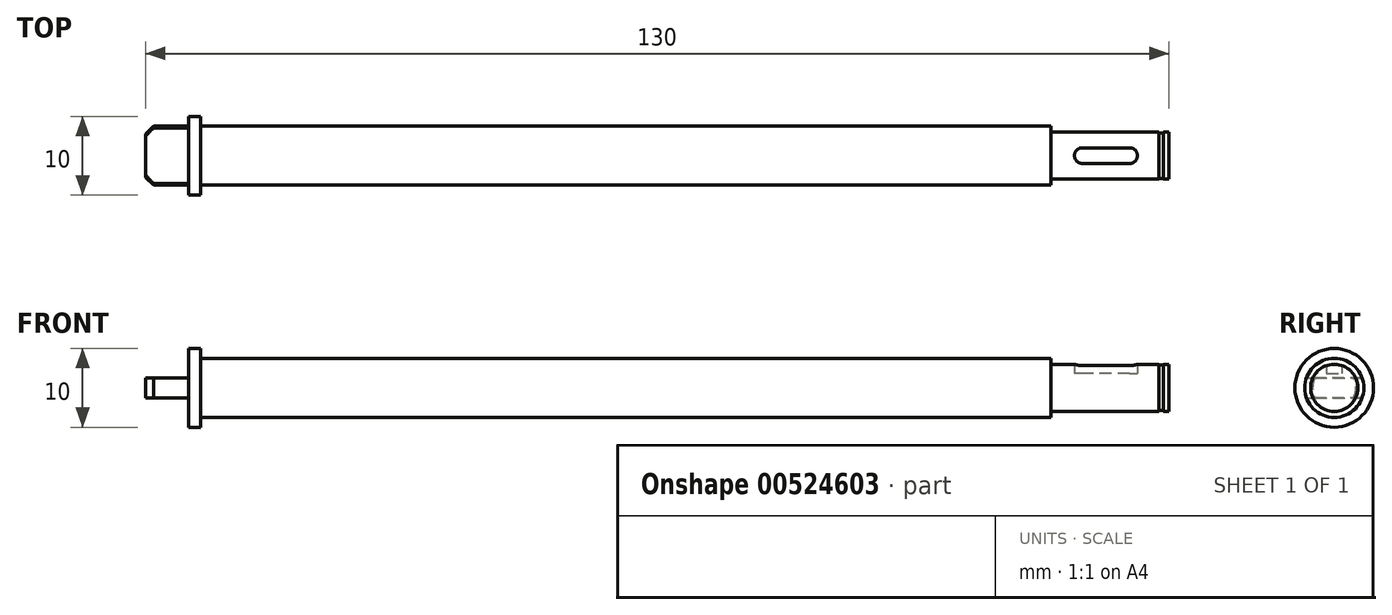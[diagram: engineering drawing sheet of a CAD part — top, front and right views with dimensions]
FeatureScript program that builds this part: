
annotation { "Feature Type Name" : "Feature", "Feature Type Description" : "" }
export const myFeature = defineFeature(function(context is Context, id is Id, definition is map)
    precondition{}
    {
        {
            var Q0;
            Q0=qCreatedBy(makeId("Front.planeOp"),FACE);
            var sketch = newSketch(context, id + "F0", { "sketchPlane" : qUnion([Q0])});
            skLineSegment(sketch, "E0", {"start": v(-31.25, 0) * mm, "end": v(193.53, 0) * mm, "construction": true});
            skLineSegment(sketch, "E1", {"start": v(0, 0) * mm, "end": v(0, 3.75) * mm});
            skLineSegment(sketch, "E2", {"start": v(0, 3.75) * mm, "end": v(5.5, 3.75) * mm});
            skLineSegment(sketch, "E3", {"start": v(5.5, 3.75) * mm, "end": v(5.5, 5) * mm});
            skLineSegment(sketch, "E4", {"start": v(5.5, 5) * mm, "end": v(7, 5) * mm});
            skLineSegment(sketch, "E5", {"start": v(7, 5) * mm, "end": v(7, 3.75) * mm});
            skLineSegment(sketch, "E6", {"start": v(7, 3.75) * mm, "end": v(115, 3.75) * mm});
            skLineSegment(sketch, "E7", {"start": v(115, 3.75) * mm, "end": v(115, 3) * mm});
            skLineSegment(sketch, "E8", {"start": v(115, 3) * mm, "end": v(128.7, 3) * mm});
            skLineSegment(sketch, "E9", {"start": v(128.7, 3) * mm, "end": v(128.7, 2.9) * mm});
            skLineSegment(sketch, "E10", {"start": v(128.7, 2.9) * mm, "end": v(129.3, 2.9) * mm});
            skLineSegment(sketch, "E11", {"start": v(129.3, 2.9) * mm, "end": v(129.3, 3) * mm});
            skLineSegment(sketch, "E12", {"start": v(129.3, 3) * mm, "end": v(130, 3) * mm});
            skLineSegment(sketch, "E13", {"start": v(130, 3) * mm, "end": v(130, 0) * mm});
            skLineSegment(sketch, "E14", {"start": v(130, 0) * mm, "end": v(0, 0) * mm});
            skSolve(sketch);
        }
        {
            var Q0;
            Q0 = qSketchRegion(id + "F0", true);
            var Q1;
            Q1=sQuery(id+"F0.wireOp",EDGE,"E0");
            revolve(context, id + "F1", {"entities" : qUnion([Q0]), "axis" : qUnion([Q1]), "revolveType" : RevolveType.FULL});
        }
        {
            var Q0;
            Q0=makeQuery(id+"F1.opRevolve","SWEPT_EDGE",EDGE,{"disambiguationData":[OSD([sQuery(id+"F0.wireOp",EDGE,"E1"),sQuery(id+"F0.wireOp",EDGE,"E2")])]});
            chamfer(context, id + "F2", {"entities" : qUnion([Q0]), "width" : 1 * mm, "tangentPropagation" : true});
        }
        {
            var Q0;
            Q0=makeQuery(id+"F1.opRevolve","SWEPT_FACE",FACE,{"disambiguationData":[OSD([sQuery(id+"F0.wireOp",EDGE,"E1")])]});
            var sketch = newSketch(context, id + "F3", { "sketchPlane" : qUnion([Q0])});
            skCircle(sketch, "E15.0", {"center": v(0, 0) * mm, "radius": 3.75 * mm});
            skLineSegment(sketch, "E16.bottom", {"start": v(3.54, 1.25) * mm, "end": v(-3.54, 1.25) * mm});
            skLineSegment(sketch, "E16.top", {"start": v(3.54, -1.25) * mm, "end": v(-3.54, -1.25) * mm});
            skSolve(sketch);
        }
        {
            var Q0;
            {var subQ0=sQuery(id+"F3.wireOp",EDGE,"E16.bottom");var subQ1=sQuery(id+"F0.wireOp",EDGE,"E1");var subQ2=makeQuery(id+"F2.opChamfer","BLEND_EDGE",EDGE,{"blendedFrom":[makeQuery(id+"F1.opRevolve","SWEPT_EDGE",EDGE,{"disambiguationData":[OSD([subQ1,sQuery(id+"F0.wireOp",EDGE,"E2")])]}),makeQuery(id+"F1.opRevolve","SWEPT_FACE",FACE,{"disambiguationData":[OSD([subQ1])]})],"blendedInto":[makeQuery(id+"F1.opRevolve","SWEPT_FACE",FACE,{"disambiguationData":[OSD([subQ1])]})]});var subQ3=makeQuery(id+"F3.imprint","INTERSECT",VERTEX,{"disambiguationData":[OD(0.0)],"derivedFrom":[subQ2,subQ0]});Q0=makeQuery(id+"F3.imprint","IMPRINT",FACE,{"disambiguationData":[TD([[makeQuery(id+"F3.imprint","IMPRINT",EDGE,{"disambiguationData":[TD([[subQ3,-1.0]])],"derivedFrom":subQ0}),-1.0]])]});}
            var Q1;
            {var subQ0=sQuery(id+"F3.wireOp",EDGE,"E16.top");var subQ1=sQuery(id+"F0.wireOp",EDGE,"E1");var subQ2=makeQuery(id+"F2.opChamfer","BLEND_EDGE",EDGE,{"blendedFrom":[makeQuery(id+"F1.opRevolve","SWEPT_EDGE",EDGE,{"disambiguationData":[OSD([subQ1,sQuery(id+"F0.wireOp",EDGE,"E2")])]}),makeQuery(id+"F1.opRevolve","SWEPT_FACE",FACE,{"disambiguationData":[OSD([subQ1])]})],"blendedInto":[makeQuery(id+"F1.opRevolve","SWEPT_FACE",FACE,{"disambiguationData":[OSD([subQ1])]})]});var subQ3=makeQuery(id+"F3.imprint","INTERSECT",VERTEX,{"disambiguationData":[OD(0.0)],"derivedFrom":[subQ2,subQ0]});Q1=makeQuery(id+"F3.imprint","IMPRINT",FACE,{"disambiguationData":[TD([[makeQuery(id+"F3.imprint","IMPRINT",EDGE,{"disambiguationData":[TD([[subQ3,-1.0]])],"derivedFrom":subQ0}),1.0]])]});}
            var Q2;
            {var subQ0=sQuery(id+"F3.wireOp",EDGE,"E16.top");var subQ1=sQuery(id+"F3.wireOp",EDGE,"E15.0");var subQ2=makeQuery(id+"F3.imprint","INTERSECT",VERTEX,{"disambiguationData":[OD(0.0)],"derivedFrom":[subQ1,subQ0]});Q2=makeQuery(id+"F3.imprint","IMPRINT",FACE,{"disambiguationData":[TD([[makeQuery(id+"F3.imprint","IMPRINT",EDGE,{"disambiguationData":[TD([[subQ2,1.0]])],"derivedFrom":subQ1}),1.0]])]});}
            var Q3;
            {var subQ0=sQuery(id+"F3.wireOp",EDGE,"E16.bottom");var subQ1=sQuery(id+"F3.wireOp",EDGE,"E15.0");var subQ2=makeQuery(id+"F3.imprint","INTERSECT",VERTEX,{"disambiguationData":[OD(0.0)],"derivedFrom":[subQ1,subQ0]});Q3=makeQuery(id+"F3.imprint","IMPRINT",FACE,{"disambiguationData":[TD([[makeQuery(id+"F3.imprint","IMPRINT",EDGE,{"disambiguationData":[TD([[subQ2,-1.0]])],"derivedFrom":subQ1}),1.0]])]});}
            var Q4;
            Q4=makeQuery(id+"F1.opRevolve","SWEPT_FACE",FACE,{"disambiguationData":[OSD([sQuery(id+"F0.wireOp",EDGE,"E3")])]});
            extrude(context, id + "F4", {"entities" : qUnion([Q0, Q1, Q2, Q3]), "operationType" : NewBodyOperationType.REMOVE, "endBound" : BoundingType.UP_TO_SURFACE, "oppositeDirection" : true, "depth" : 25 * mm, "endBoundEntityFace" : qUnion([Q4]), "offsetDistance" : 25 * mm});
        }
        {
            var Q0;
            Q0=qCreatedBy(makeId("Top.planeOp"),FACE);
            cPlane(context, id + "F5", {"entities" : qUnion([Q0]), "cplaneType" : CPlaneType.OFFSET, "offset" : (3 - 1.2) * mm, "width" : 150 * mm, "height" : 150 * mm});
        }
        {
            var Q0;
            Q0=qCreatedBy(id+"F5.planeOp",FACE);
            var sketch = newSketch(context, id + "F6", { "sketchPlane" : qUnion([Q0])});
            skLineSegment(sketch, "E17", {"start": v(125, 0) * mm, "end": v(119, 0) * mm, "construction": true});
            skArc(sketch, "E18.0.startCap", {"start": v(125, 1) * mm, "mid": v(126, 0) * mm, "end": v(125, -1) * mm});
            skArc(sketch, "E18.0.endCap", {"start": v(119, -1) * mm, "mid": v(118, 0) * mm, "end": v(119, 1) * mm});
            skLineSegment(sketch, "E18.0.left", {"start": v(125, -1) * mm, "end": v(119, -1) * mm});
            skLineSegment(sketch, "E18.0.right", {"start": v(125, 1) * mm, "end": v(119, 1) * mm});
            skSolve(sketch);
        }
        {
            var Q0;
            Q0 = qSketchRegion(id + "F6", true);
            extrude(context, id + "F7", {"entities" : qUnion([Q0]), "operationType" : NewBodyOperationType.REMOVE, "endBound" : BoundingType.UP_TO_NEXT, "depth" : 25 * mm, "offsetDistance" : 25 * mm});
        }
    });
